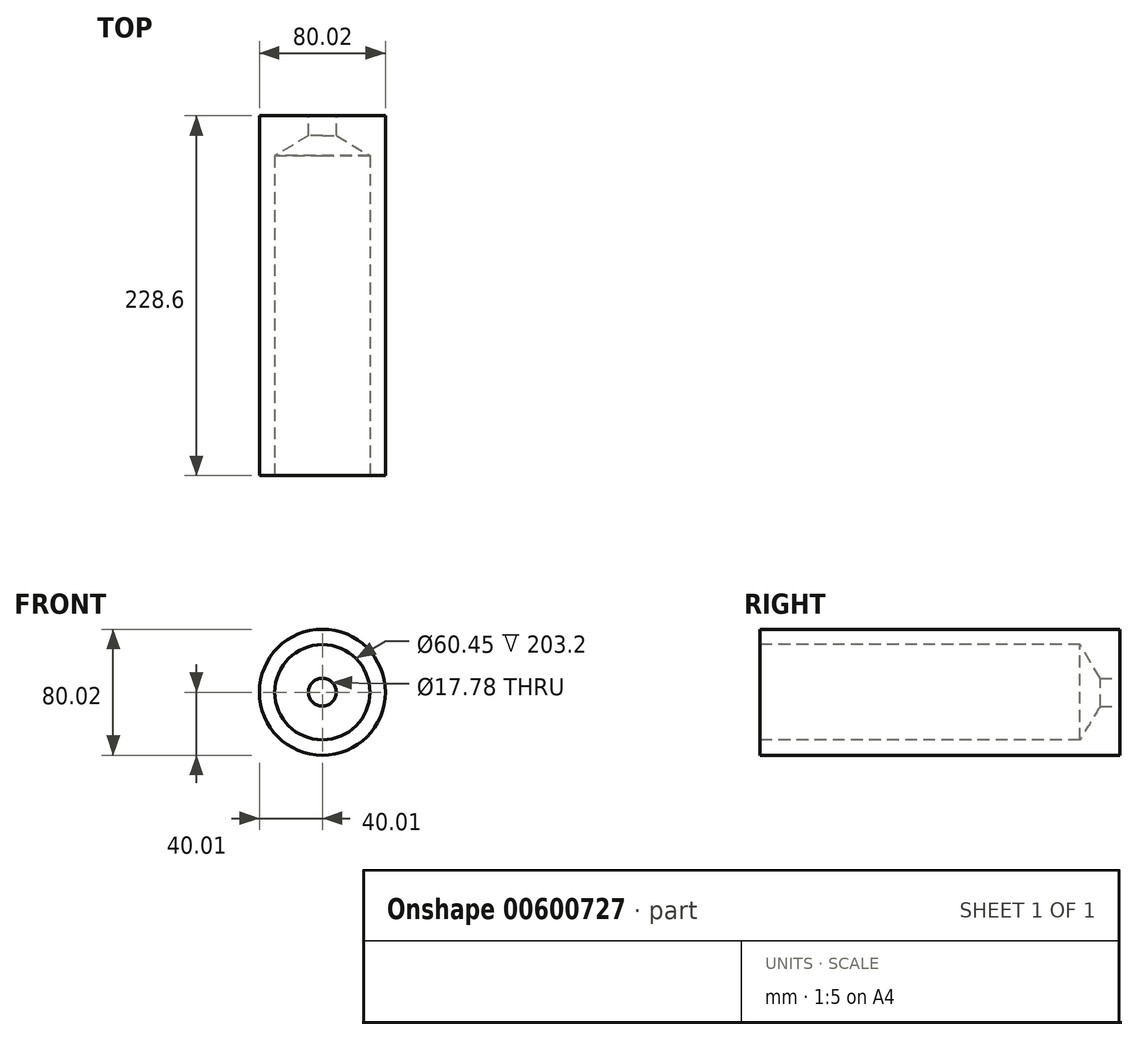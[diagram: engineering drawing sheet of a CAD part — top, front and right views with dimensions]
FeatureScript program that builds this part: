
annotation { "Feature Type Name" : "Feature", "Feature Type Description" : "" }
export const myFeature = defineFeature(function(context is Context, id is Id, definition is map)
    precondition{}
    {
        {
            var Q0;
            Q0=qCreatedBy(makeId("Front.planeOp"),FACE);
            var sketch = newSketch(context, id + "F0", { "sketchPlane" : qUnion([Q0])});
            skCircle(sketch, "E0", {"center": v(0, 0) * mm, "radius": 40 * mm});
            skSolve(sketch);
        }
        {
            var Q0;
            Q0=makeQuery(id+"F0.imprint","IMPRINT",FACE,{"disambiguationData":[TD([[makeQuery(id+"F0.imprint","IMPRINT",EDGE,{"derivedFrom":sQuery(id+"F0.wireOp",EDGE,"E0")}),1.0]])]});
            extrude(context, id + "F1", {"entities" : qUnion([Q0]), "depth" : 228.6 * mm, "offsetDistance" : 25.4 * mm});
        }
        {
            var Q0;
            Q0=makeQuery(id+"F1.opExtrude","CAP_FACE",FACE,{"disambiguationData":[OSD([sQuery(id+"F0.wireOp",EDGE,"E0")])],"isStart":false});
            var sketch = newSketch(context, id + "F2", { "sketchPlane" : qUnion([Q0])});
            skCircle(sketch, "E1", {"center": v(0, 0) * mm, "radius": 30.23 * mm});
            skSolve(sketch);
        }
        {
            var Q0;
            Q0=sQuery(id+"F2.wireOp",VERTEX,"E1.center");
            var Q1;
            Q1=makeQuery(id+"F1.opExtrude","SWEPT_BODY",BODY,{"disambiguationData":[OSD([sQuery(id+"F0.wireOp",EDGE,"E0")])]});
            hole(context, id + "F3", {"style" : HoleStyle.SIMPLE, "endStyle" : HoleEndStyle.BLIND, "holeDiameter" : 60.45 * mm, "majorDiameter" : 6.35 * mm, "holeDepth" : 203.2 * mm, "isTappedThrough" : true, "tappedDepth" : 12.7 * mm, "tapClearance" : 3, "locations" : qUnion([Q0]), "scope" : qUnion([Q1])});
        }
        {
            var Q0;
            Q0=makeQuery(id+"F1.opExtrude","CAP_FACE",FACE,{"disambiguationData":[OSD([sQuery(id+"F0.wireOp",EDGE,"E0")])],"isStart":true});
            var sketch = newSketch(context, id + "F4", { "sketchPlane" : qUnion([Q0])});
            skCircle(sketch, "E2", {"center": v(0, 0) * mm, "radius": 8.9 * mm});
            skSolve(sketch);
        }
        {
            var Q0;
            Q0=sQuery(id+"F4.wireOp",VERTEX,"E2.center");
            var Q1;
            Q1=makeQuery(id+"F1.opExtrude","SWEPT_BODY",BODY,{"disambiguationData":[OSD([sQuery(id+"F0.wireOp",EDGE,"E0")])]});
            hole(context, id + "F5", {"style" : HoleStyle.SIMPLE, "endStyle" : HoleEndStyle.THROUGH, "holeDiameter" : 17.78 * mm, "majorDiameter" : 6.35 * mm, "isTappedThrough" : true, "tappedDepth" : 12.7 * mm, "tapClearance" : 3, "locations" : qUnion([Q0]), "scope" : qUnion([Q1])});
        }
    });
